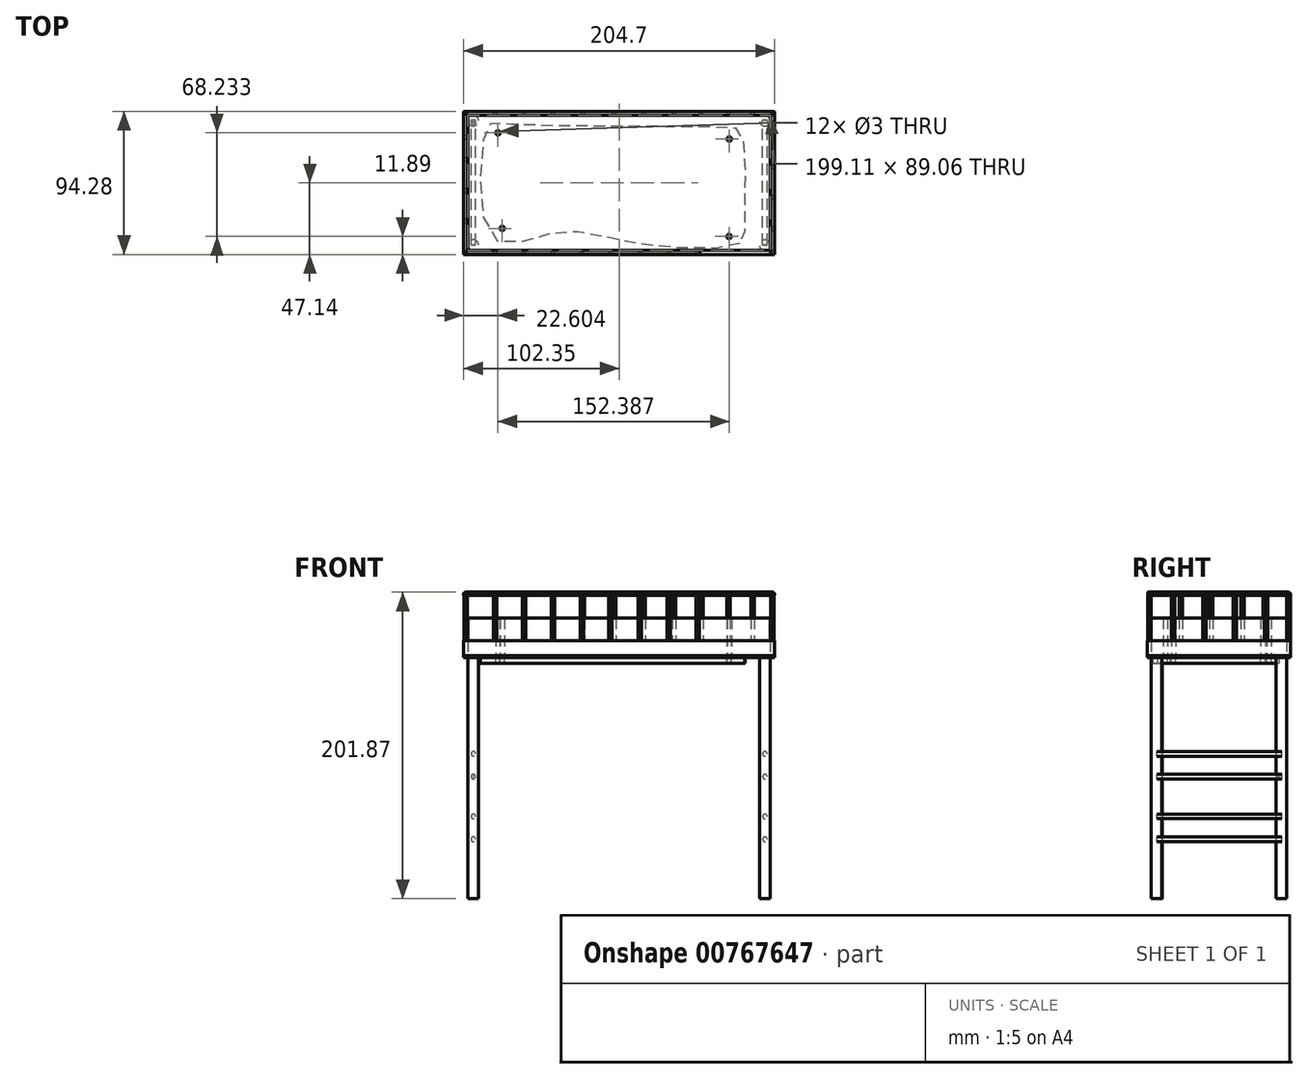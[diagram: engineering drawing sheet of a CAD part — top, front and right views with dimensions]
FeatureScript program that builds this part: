
annotation { "Feature Type Name" : "Feature", "Feature Type Description" : "" }
export const myFeature = defineFeature(function(context is Context, id is Id, definition is map)
    precondition{}
    {
        {
            var Q0;
            Q0=qCreatedBy(makeId("Top.planeOp"),FACE);
            var sketch = newSketch(context, id + "F0", { "sketchPlane" : qUnion([Q0])});
            skCircle(sketch, "E0", {"center": v(-96, 41.01) * mm, "radius": 3.5 * mm});
            skPoint(sketch, "E1.middle", {"position": v(0, 0) * mm});
            skCircle(sketch, "E2", {"center": v(96.01, 41.02) * mm, "radius": 3.5 * mm});
            skCircle(sketch, "E3", {"center": v(96.04, -41) * mm, "radius": 3.5 * mm});
            skCircle(sketch, "E4", {"center": v(-95.97, -40.92) * mm, "radius": 3.5 * mm});
            skSolve(sketch);
        }
        {
            var Q0;
            Q0 = qSketchRegion(id + "F0", true);
            extrude(context, id + "F1", {"entities" : qUnion([Q0]), "depth" : 160 * mm, "offsetDistance" : 25 * mm});
        }
        {
            var Q0;
            Q0=qCreatedBy(makeId("Top.planeOp"),FACE);
            cPlane(context, id + "F2", {"entities" : qUnion([Q0]), "cplaneType" : CPlaneType.OFFSET, "offset" : 160 * mm, "width" : 150 * mm, "height" : 150 * mm});
        }
        {
            var Q0;
            Q0=qCreatedBy(id+"F2.planeOp",FACE);
            var sketch = newSketch(context, id + "F3", { "sketchPlane" : qUnion([Q0])});
            skLineSegment(sketch, "E5.bottom", {"start": v(-102.35, 47.14) * mm, "end": v(102.35, 47.14) * mm});
            skLineSegment(sketch, "E5.top", {"start": v(-102.35, -47.14) * mm, "end": v(102.35, -47.14) * mm});
            skLineSegment(sketch, "E5.left", {"start": v(-102.35, 47.14) * mm, "end": v(-102.35, -47.14) * mm});
            skLineSegment(sketch, "E5.right", {"start": v(102.35, 47.14) * mm, "end": v(102.35, -47.14) * mm});
            skPoint(sketch, "E5.middle", {"position": v(0, 0) * mm});
            skLineSegment(sketch, "E6.bottom", {"start": v(-99.56, 44.53) * mm, "end": v(99.56, 44.53) * mm});
            skLineSegment(sketch, "E6.top", {"start": v(-99.56, -44.53) * mm, "end": v(99.56, -44.53) * mm});
            skLineSegment(sketch, "E6.left", {"start": v(-99.56, 44.53) * mm, "end": v(-99.56, -44.53) * mm});
            skLineSegment(sketch, "E6.right", {"start": v(99.56, 44.53) * mm, "end": v(99.56, -44.53) * mm});
            skSolve(sketch);
        }
        {
            var Q0;
            Q0=makeQuery(id+"F3.imprint","IMPRINT",FACE,{"disambiguationData":[TD([[makeQuery(id+"F3.imprint","IMPRINT",EDGE,{"derivedFrom":sQuery(id+"F3.wireOp",EDGE,"E5.bottom")}),-1.0]])]});
            extrude(context, id + "F4", {"entities" : qUnion([Q0]), "depth" : 10 * mm, "offsetDistance" : 25 * mm});
        }
        {
            var Q0;
            Q0=makeQuery(id+"F3.imprint","IMPRINT",FACE,{"disambiguationData":[TD([[makeQuery(id+"F3.imprint","IMPRINT",EDGE,{"derivedFrom":sQuery(id+"F3.wireOp",EDGE,"E6.bottom")}),-1.0]])]});
            extrude(context, id + "F5", {"entities" : qUnion([Q0]), "depth" : 25 * mm, "offsetDistance" : 25 * mm});
        }
        {
            var Q0;
            Q0=qCreatedBy(makeId("Front.planeOp"),FACE);
            cPlane(context, id + "F6", {"entities" : qUnion([Q0]), "cplaneType" : CPlaneType.OFFSET, "offset" : 41.4 * mm, "oppositeDirection" : true, "width" : 150 * mm, "height" : 150 * mm});
        }
        {
            var Q0;
            Q0=qCreatedBy(id+"F6.planeOp",FACE);
            var sketch = newSketch(context, id + "F7", { "sketchPlane" : qUnion([Q0])});
            skCircle(sketch, "E7", {"center": v(96.06, 95.4) * mm, "radius": 1.5 * mm});
            skCircle(sketch, "E8", {"center": v(-95.9, 95.4) * mm, "radius": 1.5 * mm});
            skCircle(sketch, "E9", {"center": v(-95.9, 80.4) * mm, "radius": 1.5 * mm});
            skCircle(sketch, "E10", {"center": v(96.06, 80.4) * mm, "radius": 1.5 * mm});
            skCircle(sketch, "E11", {"center": v(96.06, 54.15) * mm, "radius": 1.5 * mm});
            skLineSegment(sketch, "E12", {"start": v(96.06, 95.4) * mm, "end": v(96.06, 80.4) * mm});
            skLineSegment(sketch, "E13", {"start": v(-95.9, 80.4) * mm, "end": v(-95.9, 95.4) * mm});
            skLineSegment(sketch, "E14", {"start": v(96.06, 54.15) * mm, "end": v(96.06, 39.15) * mm});
            skCircle(sketch, "E15", {"center": v(96.06, 39.15) * mm, "radius": 1.5 * mm});
            skCircle(sketch, "E16", {"center": v(-95.9, 54.15) * mm, "radius": 1.5 * mm});
            skCircle(sketch, "E17", {"center": v(-95.9, 39.15) * mm, "radius": 1.5 * mm});
            skSolve(sketch);
        }
        {
            var Q0;
            Q0 = qSketchRegion(id + "F7", true);
            extrude(context, id + "F8", {"entities" : qUnion([Q0]), "depth" : 82.2 * mm, "offsetDistance" : 25 * mm});
        }
        {
            var Q0;
            Q0=makeQuery(id+"F5.opExtrude","CAP_EDGE",EDGE,{"disambiguationData":[OSD([sQuery(id+"F3.wireOp",EDGE,"E6.top")])],"isStart":false});
            var Q1;
            Q1=makeQuery(id+"F5.opExtrude","CAP_EDGE",EDGE,{"disambiguationData":[OSD([sQuery(id+"F3.wireOp",EDGE,"E6.left")])],"isStart":false});
            var Q2;
            Q2=makeQuery(id+"F5.opExtrude","SWEPT_EDGE",EDGE,{"disambiguationData":[OSD([sQuery(id+"F3.wireOp",EDGE,"E6.top"),sQuery(id+"F3.wireOp",EDGE,"E6.left")])]});
            var Q3;
            Q3=makeQuery(id+"F5.opExtrude","SWEPT_EDGE",EDGE,{"disambiguationData":[OSD([sQuery(id+"F3.wireOp",EDGE,"E6.bottom"),sQuery(id+"F3.wireOp",EDGE,"E6.left")])]});
            var Q4;
            Q4=makeQuery(id+"F5.opExtrude","CAP_EDGE",EDGE,{"disambiguationData":[OSD([sQuery(id+"F3.wireOp",EDGE,"E6.bottom")])],"isStart":false});
            var Q5;
            Q5=makeQuery(id+"F8.opExtrude","CAP_EDGE",EDGE,{"disambiguationData":[OSD([sQuery(id+"F7.wireOp",EDGE,"E9")])],"isStart":true});
            var Q6;
            Q6=makeQuery(id+"F8.opExtrude","CAP_FACE",FACE,{"disambiguationData":[OSD([sQuery(id+"F7.wireOp",EDGE,"E9")])],"isStart":true});
            var Q7;
            Q7=makeQuery(id+"F5.opExtrude","SWEPT_EDGE",EDGE,{"disambiguationData":[OSD([sQuery(id+"F3.wireOp",EDGE,"E6.bottom"),sQuery(id+"F3.wireOp",EDGE,"E6.right")])]});
            var Q8;
            Q8=makeQuery(id+"F5.opExtrude","CAP_FACE",FACE,{"disambiguationData":[OSD([sQuery(id+"F3.wireOp",EDGE,"E6.bottom"),sQuery(id+"F3.wireOp",EDGE,"E6.top"),sQuery(id+"F3.wireOp",EDGE,"E6.left"),sQuery(id+"F3.wireOp",EDGE,"E6.right")])],"isStart":false});
            var Q9;
            Q9=makeQuery(id+"F5.opExtrude","SWEPT_EDGE",EDGE,{"disambiguationData":[OSD([sQuery(id+"F3.wireOp",EDGE,"E6.top"),sQuery(id+"F3.wireOp",EDGE,"E6.right")])]});
            var Q10;
            Q10=makeQuery(id+"F5.opExtrude","CAP_EDGE",EDGE,{"disambiguationData":[OSD([sQuery(id+"F3.wireOp",EDGE,"E6.right")])],"isStart":false});
            fillet(context, id + "F9", {"entities" : qUnion([Q0, Q1, Q2, Q3, Q4, Q5, Q6, Q7, Q8, Q9, Q10]), "radius" : 1.42 * mm, "tangentPropagation" : true, "allowEdgeOverflow" : false});
        }
        {
            var Q0;
            Q0=makeQuery(id+"F4.opExtrude","CAP_FACE",FACE,{"disambiguationData":[OSD([sQuery(id+"F3.wireOp",EDGE,"E5.bottom"),sQuery(id+"F3.wireOp",EDGE,"E5.top"),sQuery(id+"F3.wireOp",EDGE,"E5.left"),sQuery(id+"F3.wireOp",EDGE,"E5.right"),sQuery(id+"F3.wireOp",EDGE,"E6.bottom"),sQuery(id+"F3.wireOp",EDGE,"E6.top"),sQuery(id+"F3.wireOp",EDGE,"E6.left"),sQuery(id+"F3.wireOp",EDGE,"E6.right")])],"isStart":false});
            var sketch = newSketch(context, id + "F10", { "sketchPlane" : qUnion([Q0])});
            skCircle(sketch, "E18", {"center": v(-81.67, -45.85) * mm, "radius": 1.1 * mm});
            skCircle(sketch, "E19", {"center": v(-62.7, -45.85) * mm, "radius": 1.1 * mm});
            skCircle(sketch, "E20", {"center": v(-43.53, -45.85) * mm, "radius": 1.1 * mm});
            skCircle(sketch, "E21", {"center": v(-24.57, -45.88) * mm, "radius": 1.1 * mm});
            skCircle(sketch, "E22", {"center": v(-5.66, -45.88) * mm, "radius": 1.1 * mm});
            skCircle(sketch, "E23", {"center": v(13.53, -45.88) * mm, "radius": 1.1 * mm});
            skCircle(sketch, "E24", {"center": v(32.77, -45.88) * mm, "radius": 1.1 * mm});
            skCircle(sketch, "E25", {"center": v(51.79, -45.84) * mm, "radius": 1.1 * mm});
            skCircle(sketch, "E26", {"center": v(101, -45.83) * mm, "radius": 1.1 * mm});
            skCircle(sketch, "E27", {"center": v(-81.67, 45.83) * mm, "radius": 1.1 * mm});
            skCircle(sketch, "E28", {"center": v(-62.7, 45.83) * mm, "radius": 1.1 * mm});
            skCircle(sketch, "E29", {"center": v(-43.53, 45.83) * mm, "radius": 1.1 * mm});
            skCircle(sketch, "E30", {"center": v(-23.85, 45.89) * mm, "radius": 1.1 * mm});
            skCircle(sketch, "E31", {"center": v(-3.2, 45.79) * mm, "radius": 1.1 * mm});
            skCircle(sketch, "E32", {"center": v(16.2, 45.9) * mm, "radius": 1.1 * mm});
            skCircle(sketch, "E33", {"center": v(36.12, 45.82) * mm, "radius": 1.1 * mm});
            skCircle(sketch, "E34", {"center": v(54.15, 45.82) * mm, "radius": 1.1 * mm});
            skCircle(sketch, "E35", {"center": v(72.05, 45.81) * mm, "radius": 1.1 * mm});
            skCircle(sketch, "E36", {"center": v(87.98, 45.86) * mm, "radius": 1.1 * mm});
            skCircle(sketch, "E37", {"center": v(100.93, 45.74) * mm, "radius": 1.1 * mm});
            skCircle(sketch, "E38", {"center": v(100.97, 31.05) * mm, "radius": 1.1 * mm});
            skCircle(sketch, "E39", {"center": v(101, 10.57) * mm, "radius": 1.1 * mm});
            skCircle(sketch, "E40", {"center": v(100.98, -9.62) * mm, "radius": 1.1 * mm});
            skCircle(sketch, "E41", {"center": v(100.94, -30.21) * mm, "radius": 1.1 * mm});
            skCircle(sketch, "E42", {"center": v(-101.03, 30.13) * mm, "radius": 1.1 * mm});
            skCircle(sketch, "E43", {"center": v(-101, 15.44) * mm, "radius": 1.1 * mm});
            skCircle(sketch, "E44", {"center": v(-100.96, -5.04) * mm, "radius": 1.1 * mm});
            skCircle(sketch, "E45", {"center": v(-100.99, -25.24) * mm, "radius": 1.1 * mm});
            skCircle(sketch, "E46", {"center": v(-101.03, -45.83) * mm, "radius": 1.1 * mm});
            skCircle(sketch, "E47", {"center": v(-101.03, 45.83) * mm, "radius": 1.1 * mm});
            skSolve(sketch);
        }
        {
            var Q0;
            Q0 = qSketchRegion(id + "F10", true);
            extrude(context, id + "F11", {"entities" : qUnion([Q0]), "operationType" : NewBodyOperationType.ADD, "depth" : 30 * mm, "offsetDistance" : 25 * mm});
        }
        {
            var Q0;
            Q0=makeQuery(id+"F5.opExtrude","CAP_FACE",FACE,{"disambiguationData":[OSD([sQuery(id+"F3.wireOp",EDGE,"E6.bottom"),sQuery(id+"F3.wireOp",EDGE,"E6.top"),sQuery(id+"F3.wireOp",EDGE,"E6.left"),sQuery(id+"F3.wireOp",EDGE,"E6.right")])],"isStart":false});
            cPlane(context, id + "F12", {"entities" : qUnion([Q0]), "cplaneType" : CPlaneType.OFFSET, "offset" : 14.67 * mm, "width" : 150 * mm, "height" : 150 * mm});
        }
        {
            var Q0;
            Q0=qCreatedBy(id+"F12.planeOp",FACE);
            var sketch = newSketch(context, id + "F13", { "sketchPlane" : qUnion([Q0])});
            skLineSegment(sketch, "E48.bottom", {"start": v(-102.35, -47) * mm, "end": v(53.1, -47) * mm});
            skLineSegment(sketch, "E48.top", {"start": v(-102.35, 47) * mm, "end": v(102.35, 47) * mm});
            skLineSegment(sketch, "E48.left", {"start": v(-102.35, -47) * mm, "end": v(-102.35, 47) * mm});
            skLineSegment(sketch, "E48.right", {"start": v(102.35, -47) * mm, "end": v(102.35, 47) * mm});
            skPoint(sketch, "E48.middle", {"position": v(0, 0) * mm});
            skLineSegment(sketch, "E49.bottom", {"start": v(-99.85, -44.49) * mm, "end": v(53.1, -44.49) * mm});
            skLineSegment(sketch, "E49.top", {"start": v(-99.85, 44.49) * mm, "end": v(99.85, 44.49) * mm});
            skLineSegment(sketch, "E49.left", {"start": v(-99.85, -44.49) * mm, "end": v(-99.85, 44.49) * mm});
            skLineSegment(sketch, "E49.right", {"start": v(99.85, -44.49) * mm, "end": v(99.85, 44.49) * mm});
            skLineSegment(sketch, "E50", {"start": v(53.1, -47) * mm, "end": v(53.1, -44.49) * mm});
            skLineSegment(sketch, "E51", {"start": v(99.85, -44.49) * mm, "end": v(99.85, -47) * mm});
            skLineSegment(sketch, "E52", {"start": v(99.85, -47) * mm, "end": v(102.35, -47) * mm});
            skSolve(sketch);
        }
        {
            var Q0;
            Q0=makeQuery(id+"F13.imprint","IMPRINT",FACE,{"disambiguationData":[TD([[makeQuery(id+"F13.imprint","IMPRINT",EDGE,{"derivedFrom":sQuery(id+"F13.wireOp",EDGE,"E48.bottom")}),1.0]])]});
            extrude(context, id + "F14", {"entities" : qUnion([Q0]), "operationType" : NewBodyOperationType.ADD, "depth" : 2.2 * mm, "offsetDistance" : 25 * mm});
        }
        {
            var Q0;
            Q0=makeQuery(id+"F14.opExtrude","CAP_EDGE",EDGE,{"disambiguationData":[OSD([sQuery(id+"F13.wireOp",EDGE,"E48.top")])],"isStart":false});
            var Q1;
            Q1=makeQuery(id+"F14.opExtrude","CAP_EDGE",EDGE,{"disambiguationData":[OSD([sQuery(id+"F13.wireOp",EDGE,"E48.right")])],"isStart":false});
            var Q2;
            Q2=makeQuery(id+"F14.opExtrude","CAP_EDGE",EDGE,{"disambiguationData":[OSD([sQuery(id+"F13.wireOp",EDGE,"E48.bottom")])],"isStart":false});
            var Q3;
            Q3=makeQuery(id+"F14.opExtrude","CAP_EDGE",EDGE,{"disambiguationData":[OSD([sQuery(id+"F13.wireOp",EDGE,"E48.left")])],"isStart":false});
            fillet(context, id + "F15", {"entities" : qUnion([Q0, Q1, Q2, Q3]), "radius" : 1.1 * mm, "tangentPropagation" : true, "allowEdgeOverflow" : false});
        }
        {
            var Q0;
            Q0=makeQuery(id+"F14.opExtrude","CAP_EDGE",EDGE,{"disambiguationData":[OSD([sQuery(id+"F13.wireOp",EDGE,"E49.right"),sQuery(id+"F13.wireOp",EDGE,"E51")])],"isStart":false});
            var Q1;
            Q1=makeQuery(id+"F14.opExtrude","CAP_EDGE",EDGE,{"disambiguationData":[OSD([sQuery(id+"F13.wireOp",EDGE,"E49.top")])],"isStart":false});
            var Q2;
            Q2=makeQuery(id+"F14.opExtrude","CAP_EDGE",EDGE,{"disambiguationData":[OSD([sQuery(id+"F13.wireOp",EDGE,"E49.left")])],"isStart":false});
            var Q3;
            Q3=makeQuery(id+"F14.opExtrude","CAP_EDGE",EDGE,{"disambiguationData":[OSD([sQuery(id+"F13.wireOp",EDGE,"E49.bottom")])],"isStart":false});
            fillet(context, id + "F16", {"entities" : qUnion([Q0, Q1, Q2, Q3]), "radius" : 1.4 * mm, "tangentPropagation" : true, "allowEdgeOverflow" : false});
        }
        {
            var Q0;
            Q0=makeQuery(id+"F15.opFillet","BLEND_EDGE",EDGE,{"blendedFrom":[makeQuery(id+"F14.opExtrude","CAP_EDGE",EDGE,{"disambiguationData":[OSD([sQuery(id+"F13.wireOp",EDGE,"E48.right")])],"isStart":false}),makeQuery(id+"F14.opExtrude","SWEPT_FACE",FACE,{"disambiguationData":[OSD([sQuery(id+"F13.wireOp",EDGE,"E52")])]})],"blendedInto":[makeQuery(id+"F14.opExtrude","SWEPT_FACE",FACE,{"disambiguationData":[OSD([sQuery(id+"F13.wireOp",EDGE,"E52")])]})]});
            var Q1;
            Q1=makeQuery(id+"F16.opFillet","BLEND_EDGE",EDGE,{"blendedFrom":[makeQuery(id+"F14.opExtrude","CAP_EDGE",EDGE,{"disambiguationData":[OSD([sQuery(id+"F13.wireOp",EDGE,"E49.right"),sQuery(id+"F13.wireOp",EDGE,"E51")])],"isStart":false}),makeQuery(id+"F14.opExtrude","SWEPT_FACE",FACE,{"disambiguationData":[OSD([sQuery(id+"F13.wireOp",EDGE,"E52")])]})],"blendedInto":[makeQuery(id+"F14.opExtrude","SWEPT_FACE",FACE,{"disambiguationData":[OSD([sQuery(id+"F13.wireOp",EDGE,"E52")])]})]});
            var Q2;
            Q2=makeQuery(id+"F14.opExtrude","SWEPT_EDGE",EDGE,{"disambiguationData":[OSD([sQuery(id+"F13.wireOp",EDGE,"E51"),sQuery(id+"F13.wireOp",EDGE,"E52")])]});
            var Q3;
            Q3=makeQuery(id+"F14.opExtrude","CAP_EDGE",EDGE,{"disambiguationData":[OSD([sQuery(id+"F13.wireOp",EDGE,"E52")])],"isStart":true});
            var Q4;
            Q4=makeQuery(id+"F14.opExtrude","SWEPT_EDGE",EDGE,{"disambiguationData":[OSD([sQuery(id+"F13.wireOp",EDGE,"E48.right"),sQuery(id+"F13.wireOp",EDGE,"E52")])]});
            fillet(context, id + "F17", {"entities" : qUnion([Q0, Q1, Q2, Q3, Q4]), "radius" : 0.39 * mm, "tangentPropagation" : true, "allowEdgeOverflow" : false});
        }
        {
            var Q0;
            Q0=makeQuery(id+"F14.opExtrude","CAP_EDGE",EDGE,{"disambiguationData":[OSD([sQuery(id+"F13.wireOp",EDGE,"E50")])],"isStart":true});
            var Q1;
            Q1=makeQuery(id+"F15.opFillet","BLEND_EDGE",EDGE,{"blendedFrom":[makeQuery(id+"F14.opExtrude","CAP_EDGE",EDGE,{"disambiguationData":[OSD([sQuery(id+"F13.wireOp",EDGE,"E48.bottom")])],"isStart":false}),makeQuery(id+"F14.opExtrude","SWEPT_FACE",FACE,{"disambiguationData":[OSD([sQuery(id+"F13.wireOp",EDGE,"E50")])]})],"blendedInto":[makeQuery(id+"F14.opExtrude","SWEPT_FACE",FACE,{"disambiguationData":[OSD([sQuery(id+"F13.wireOp",EDGE,"E50")])]})]});
            var Q2;
            Q2=makeQuery(id+"F16.opFillet","BLEND_EDGE",EDGE,{"blendedFrom":[makeQuery(id+"F14.opExtrude","CAP_EDGE",EDGE,{"disambiguationData":[OSD([sQuery(id+"F13.wireOp",EDGE,"E49.bottom")])],"isStart":false}),makeQuery(id+"F14.opExtrude","SWEPT_FACE",FACE,{"disambiguationData":[OSD([sQuery(id+"F13.wireOp",EDGE,"E50")])]})],"blendedInto":[makeQuery(id+"F14.opExtrude","SWEPT_FACE",FACE,{"disambiguationData":[OSD([sQuery(id+"F13.wireOp",EDGE,"E50")])]})]});
            var Q3;
            Q3=makeQuery(id+"F14.opExtrude","SWEPT_EDGE",EDGE,{"disambiguationData":[OSD([sQuery(id+"F13.wireOp",EDGE,"E49.bottom"),sQuery(id+"F13.wireOp",EDGE,"E50")])]});
            var Q4;
            Q4=makeQuery(id+"F14.opExtrude","SWEPT_EDGE",EDGE,{"disambiguationData":[OSD([sQuery(id+"F13.wireOp",EDGE,"E48.bottom"),sQuery(id+"F13.wireOp",EDGE,"E50")])]});
            fillet(context, id + "F18", {"entities" : qUnion([Q0, Q1, Q2, Q3, Q4]), "radius" : 0.39 * mm, "tangentPropagation" : true, "allowEdgeOverflow" : false});
        }
        {
            var Q0;
            Q0=makeQuery(id+"F3.imprint","IMPRINT",FACE,{"disambiguationData":[TD([[makeQuery(id+"F3.imprint","IMPRINT",EDGE,{"derivedFrom":sQuery(id+"F3.wireOp",EDGE,"E6.bottom")}),-1.0]])]});
            var Q1;
            Q1=makeQuery(id+"F3.imprint","IMPRINT",FACE,{"disambiguationData":[TD([[makeQuery(id+"F3.imprint","IMPRINT",EDGE,{"derivedFrom":sQuery(id+"F3.wireOp",EDGE,"E5.bottom")}),-1.0]])]});
            extrude(context, id + "F19", {"entities" : qUnion([Q0, Q1]), "oppositeDirection" : true, "depth" : 1 * mm, "offsetDistance" : 25 * mm});
        }
        {
            var Q0;
            Q0=makeQuery(id+"F19.opExtrude","CAP_FACE",FACE,{"disambiguationData":[OSD([sQuery(id+"F3.wireOp",EDGE,"E5.bottom"),sQuery(id+"F3.wireOp",EDGE,"E5.top"),sQuery(id+"F3.wireOp",EDGE,"E5.left"),sQuery(id+"F3.wireOp",EDGE,"E5.right")])],"isStart":false});
            var sketch = newSketch(context, id + "F20", { "sketchPlane" : qUnion([Q0])});
            skFitSpline(sketch, "E53", {"points": [v(79.49, 39.87) * mm, v(8.18, 39.3) * mm, v(-42.29, 32.78) * mm, v(-82.96, 36.14) * mm, v(-87.09, -35.9) * mm, v(-75.94, -39.24) * mm, v(65.46, -37.2) * mm, v(81.17, -30.7) * mm, v(82.54, 26.71) * mm, v(79.49, 39.87) * mm]});
            skCircle(sketch, "E54", {"center": v(-76.93, 29.94) * mm, "radius": 1.5 * mm});
            skCircle(sketch, "E55", {"center": v(72.42, 35.25) * mm, "radius": 1.5 * mm});
            skCircle(sketch, "E56", {"center": v(72.64, -28.98) * mm, "radius": 1.5 * mm});
            skCircle(sketch, "E57", {"center": v(-79.75, -32.98) * mm, "radius": 1.5 * mm});
            skSolve(sketch);
        }
        {
            var Q0;
            Q0=makeQuery(id+"F20.imprint","IMPRINT",FACE,{"disambiguationData":[TD([[makeQuery(id+"F20.imprint","IMPRINT",EDGE,{"derivedFrom":sQuery(id+"F20.wireOp",EDGE,"E53")}),1.0]])]});
            extrude(context, id + "F21", {"entities" : qUnion([Q0]), "depth" : 4 * mm, "offsetDistance" : 25 * mm});
        }
        {
            var Q0;
            Q0=makeQuery(id+"F20.imprint","IMPRINT",FACE,{"disambiguationData":[TD([[makeQuery(id+"F20.imprint","IMPRINT",EDGE,{"derivedFrom":sQuery(id+"F20.wireOp",EDGE,"E54")}),1.0]])]});
            var Q1;
            Q1=makeQuery(id+"F20.imprint","IMPRINT",FACE,{"disambiguationData":[TD([[makeQuery(id+"F20.imprint","IMPRINT",EDGE,{"derivedFrom":sQuery(id+"F20.wireOp",EDGE,"E57")}),1.0]])]});
            var Q2;
            Q2=makeQuery(id+"F20.imprint","IMPRINT",FACE,{"disambiguationData":[TD([[makeQuery(id+"F20.imprint","IMPRINT",EDGE,{"derivedFrom":sQuery(id+"F20.wireOp",EDGE,"E56")}),1.0]])]});
            var Q3;
            Q3=makeQuery(id+"F20.imprint","IMPRINT",FACE,{"disambiguationData":[TD([[makeQuery(id+"F20.imprint","IMPRINT",EDGE,{"derivedFrom":sQuery(id+"F20.wireOp",EDGE,"E55")}),1.0]])]});
            extrude(context, id + "F22", {"entities" : qUnion([Q0, Q1, Q2, Q3]), "operationType" : NewBodyOperationType.REMOVE, "oppositeDirection" : true, "depth" : 46.1 * mm, "offsetDistance" : 25 * mm});
        }
    });
